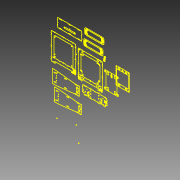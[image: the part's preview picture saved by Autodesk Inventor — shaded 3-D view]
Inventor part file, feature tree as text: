
AUTODESK INVENTOR PART (.ipt)
format: ipt  version: 2013 (Build 170138000, 138)  size: 409,088 bytes
history: native  units: in
note: dims shown in document units (in); Inventor stores cm internally (conversion verified against a paired STEP export)
features: reference x14, sketch x1
ambient origin geometry x8: Origin, YZ Plane, XZ Plane, XY Plane, X Axis, Y Axis, Z Axis, Center Point
feature tree (15):
  sketch  "Sketch1"
  reference  "Reference1"
  reference  "Reference2"
  reference  "Reference3"
  reference  "Reference4"
  reference  "Reference5"
  reference  "Reference6"
  reference  "Reference7"
  reference  "Reference8"
  reference  "Reference9"
  reference  "Reference10"
  reference  "Reference11"
  reference  "Reference12"
  reference  "Reference13"
  reference  "Reference14"
